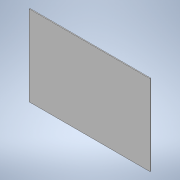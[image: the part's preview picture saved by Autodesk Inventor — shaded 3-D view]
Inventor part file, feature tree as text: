
AUTODESK INVENTOR PART (.ipt)
format: ipt  version: 2021 (Build 250183000, 183)  size: 87,040 bytes
history: native  units: mm
features: extrude x1, sketch x1
ambient origin geometry x8: Origin, YZ Plane, XZ Plane, XY Plane, X Axis, Y Axis, Z Axis, Center Point
bodies: Solid1 (feature_tree)
feature tree (2):
  extrude  "Extrusion1"  Depth=300.0mm
  sketch  "Sketch1"  dims[d0=200.0mm d1=300.0mm d2=2.0mm d3=0.0mm]
